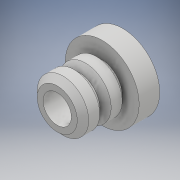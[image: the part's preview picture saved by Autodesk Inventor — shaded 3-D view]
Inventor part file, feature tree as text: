
AUTODESK INVENTOR PART (.ipt)
format: ipt  version: 2017 (Build 210142000, 142)  size: 272,896 bytes
history: native  units: mm
features: sketch x3, extrude x2, revolve x1, hole x1
ambient origin geometry x8: Origin, YZ Plane, XZ Plane, XY Plane, X Axis, Y Axis, Z Axis, Center Point
bodies: Solid1 (feature_tree)
feature tree (7):
  extrude  "Extrusion1"  Depth=7.0mm TaperAngle=0.0deg
  extrude  "Extrusion2"  Depth=3.2mm TaperAngle=0.0deg
  revolve  "Revolution1"  [1 undecoded]
  hole  "Hole2"  [1 undecoded]
  sketch  "Sketch1"  dims[d0=8.0mm d1=7.0mm d2=0.0mm]
  sketch  "Sketch2"  dims[d3=11.5mm d4=3.2mm d5=0.0mm]
  sketch  "Sketch4"  dims[d23=90.0deg d24=10.0mm d25=10.0mm d26=4.4mm d27=6.0mm d28=4.0mm d29=2.0mm d30=90.0deg d31=8.0mm d32=20.594885mm]
note: 2 required parameter values undecoded (feature->parameter linkage not recoverable at this tier; creation-order binding heuristic only, values carry confidence <= 0.55)